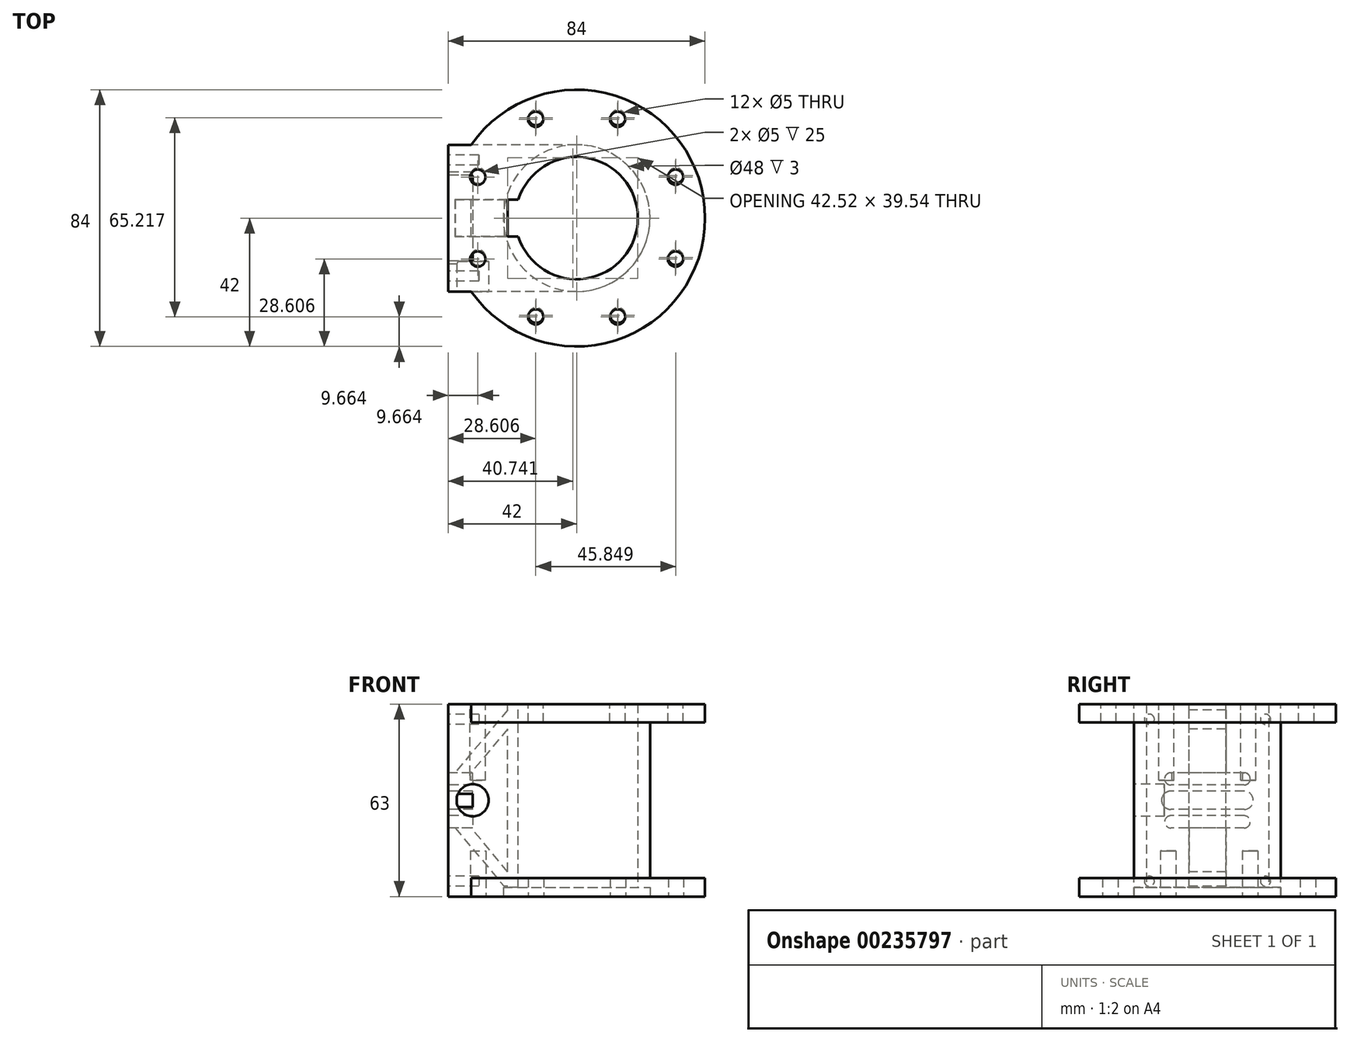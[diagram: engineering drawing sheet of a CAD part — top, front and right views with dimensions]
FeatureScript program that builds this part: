
annotation { "Feature Type Name" : "Feature", "Feature Type Description" : "" }
export const myFeature = defineFeature(function(context is Context, id is Id, definition is map)
    precondition{}
    {
        {
            var Q0;
            Q0=qCreatedBy(makeId("Top.planeOp"),FACE);
            var sketch = newSketch(context, id + "F0", { "sketchPlane" : qUnion([Q0])});
            skCircle(sketch, "E0", {"center": v(0, 0) * mm, "radius": 42 * mm});
            skSolve(sketch);
        }
        {
            var Q0;
            Q0=makeQuery(id+"F0.imprint","IMPRINT",FACE,{"disambiguationData":[TD([[makeQuery(id+"F0.imprint","IMPRINT",EDGE,{"derivedFrom":sQuery(id+"F0.wireOp",EDGE,"E0")}),1.0]])]});
            extrude(context, id + "F1", {"entities" : qUnion([Q0]), "depth" : 6 * mm});
        }
        {
            var Q0;
            Q0=makeQuery(id+"F1.opExtrude","CAP_FACE",FACE,{"disambiguationData":[OSD([sQuery(id+"F0.wireOp",EDGE,"E0")])],"isStart":false});
            var sketch = newSketch(context, id + "F2", { "sketchPlane" : qUnion([Q0])});
            skCircle(sketch, "E1", {"center": v(0, 0) * mm, "radius": 24 * mm});
            skLineSegment(sketch, "E2", {"start": v(0, 24) * mm, "end": v(-42, 24) * mm});
            skLineSegment(sketch, "E3.MirrorCS", {"start": v(0, -24) * mm, "end": v(-42, -24) * mm});
            skLineSegment(sketch, "E4", {"start": v(-42, 24) * mm, "end": v(-42, -24) * mm});
            skSolve(sketch);
        }
        {
            var Q0;
            {var subQ0=sQuery(id+"F2.wireOp",EDGE,"E4");var subQ1=sQuery(id+"F2.wireOp",EDGE,"E2");var subQ2=makeQuery(id+"F2.imprint","INTERSECT",VERTEX,{"derivedFrom":[subQ1,subQ0]});Q0=makeQuery(id+"F2.imprint","IMPRINT",FACE,{"disambiguationData":[TD([[makeQuery(id+"F2.imprint","IMPRINT",EDGE,{"disambiguationData":[TD([[subQ2,1.0]])],"derivedFrom":subQ1}),1.0]])]});}
            var Q1;
            {var subQ0=sQuery(id+"F2.wireOp",EDGE,"E4");var subQ1=sQuery(id+"F2.wireOp",EDGE,"E3.MirrorCS");var subQ2=makeQuery(id+"F2.imprint","INTERSECT",VERTEX,{"derivedFrom":[subQ1,subQ0]});Q1=makeQuery(id+"F2.imprint","IMPRINT",FACE,{"disambiguationData":[TD([[makeQuery(id+"F2.imprint","IMPRINT",EDGE,{"disambiguationData":[TD([[subQ2,1.0]])],"derivedFrom":subQ1}),-1.0]])]});}
            extrude(context, id + "F3", {"entities" : qUnion([Q0, Q1]), "operationType" : NewBodyOperationType.ADD, "oppositeDirection" : true, "depth" : 6 * mm});
        }
        {
            var Q0;
            {var subQ0=sQuery(id+"F2.wireOp",EDGE,"E1");var subQ1=makeQuery(id+"F2.imprint","INTERSECT",VERTEX,{"derivedFrom":[subQ0,sQuery(id+"F2.wireOp",EDGE,"E2")]});Q0=makeQuery(id+"F2.imprint","IMPRINT",FACE,{"disambiguationData":[TD([[makeQuery(id+"F2.imprint","IMPRINT",EDGE,{"disambiguationData":[TD([[subQ1,-1.0]])],"derivedFrom":subQ0}),1.0]])]});}
            var Q1;
            {var subQ1=sQuery(id+"F2.wireOp",EDGE,"E1");var subQ6=sQuery(id+"F2.wireOp",EDGE,"E2");var subQ8=makeQuery(id+"F2.imprint","INTERSECT",VERTEX,{"derivedFrom":[subQ1,subQ6]});Q1=makeQuery(id+"F2.imprint","IMPRINT",FACE,{"disambiguationData":[TD([[makeQuery(id+"F2.imprint","IMPRINT",EDGE,{"disambiguationData":[TD([[subQ8,-1.0]])],"derivedFrom":subQ1}),-1.0]])]});}
            var Q2;
            {var subQ0=sQuery(id+"F2.wireOp",EDGE,"E4");var subQ1=sQuery(id+"F2.wireOp",EDGE,"E3.MirrorCS");var subQ2=makeQuery(id+"F2.imprint","INTERSECT",VERTEX,{"derivedFrom":[subQ1,subQ0]});Q2=makeQuery(id+"F2.imprint","IMPRINT",FACE,{"disambiguationData":[TD([[makeQuery(id+"F2.imprint","IMPRINT",EDGE,{"disambiguationData":[TD([[subQ2,1.0]])],"derivedFrom":subQ1}),-1.0]])]});}
            var Q3;
            {var subQ0=sQuery(id+"F2.wireOp",EDGE,"E4");var subQ1=sQuery(id+"F2.wireOp",EDGE,"E2");var subQ2=makeQuery(id+"F2.imprint","INTERSECT",VERTEX,{"derivedFrom":[subQ1,subQ0]});Q3=makeQuery(id+"F2.imprint","IMPRINT",FACE,{"disambiguationData":[TD([[makeQuery(id+"F2.imprint","IMPRINT",EDGE,{"disambiguationData":[TD([[subQ2,1.0]])],"derivedFrom":subQ1}),1.0]])]});}
            extrude(context, id + "F4", {"entities" : qUnion([Q0, Q1, Q2, Q3]), "operationType" : NewBodyOperationType.ADD, "depth" : 57 * mm});
        }
        {
            var Q0;
            Q0=makeQuery(id+"F4.opExtrude","CAP_FACE",FACE,{"disambiguationData":[OSD([sQuery(id+"F2.wireOp",EDGE,"E1"),sQuery(id+"F2.wireOp",EDGE,"E2"),sQuery(id+"F2.wireOp",EDGE,"E3.MirrorCS"),sQuery(id+"F2.wireOp",EDGE,"E4")])],"isStart":false});
            var sketch = newSketch(context, id + "F5", { "sketchPlane" : qUnion([Q0])});
            skCircle(sketch, "E5", {"center": v(0, 0) * mm, "radius": 42 * mm});
            skSolve(sketch);
        }
        {
            var Q0;
            {var subQ5=makeQuery(id+"F4.opExtrude","CAP_EDGE",EDGE,{"disambiguationData":[OSD([sQuery(id+"F2.wireOp",EDGE,"E1")])],"isStart":false});Q0=makeQuery(id+"F5.imprint","IMPRINT",FACE,{"disambiguationData":[TD([[makeQuery(id+"F5.imprint","IMPRINT",EDGE,{"derivedFrom":subQ5}),-1.0]])]});}
            extrude(context, id + "F6", {"entities" : qUnion([Q0]), "operationType" : NewBodyOperationType.ADD, "oppositeDirection" : true, "depth" : 6 * mm});
        }
        {
            var Q0;
            {var subQ0=sQuery(id+"F2.wireOp",EDGE,"E4");var subQ1=sQuery(id+"F0.wireOp",EDGE,"E0");Q0=makeQuery(id+"F3.boolean.opBoolean","MERGE",FACE,{"derivedFrom":[makeQuery(id+"F1.opExtrude","CAP_FACE",FACE,{"disambiguationData":[OSD([subQ1])],"isStart":true}),makeQuery(id+"F3.opExtrude","CAP_FACE",FACE,{"disambiguationData":[OSD([subQ1,sQuery(id+"F2.wireOp",EDGE,"E2"),subQ0])],"isStart":false}),makeQuery(id+"F3.opExtrude","CAP_FACE",FACE,{"disambiguationData":[OSD([subQ1,sQuery(id+"F2.wireOp",EDGE,"E3.MirrorCS"),subQ0])],"isStart":false})]});}
            var sketch = newSketch(context, id + "F7", { "sketchPlane" : qUnion([Q0])});
            skPoint(sketch, "E6", {"position": v(0, 0) * mm});
            skSolve(sketch);
        }
        {
            var Q0;
            Q0=sQuery(id+"F7.wireOp",VERTEX,"E6");
            var Q1;
            Q1=makeQuery(id+"F1.opExtrude","SWEPT_BODY",BODY,{"disambiguationData":[OSD([sQuery(id+"F0.wireOp",EDGE,"E0")])]});
            hole(context, id + "F8", {"style" : HoleStyle.C_BORE, "endStyle" : HoleEndStyle.BLIND, "holeDiameter" : 40 * mm, "cBoreDiameter" : 48 * mm, "cBoreDepth" : 3 * mm, "holeDepth" : 63 * mm, "tappedDepth" : 20 * mm, "tapClearance" : 6, "startFromSketch" : true, "locations" : qUnion([Q0]), "scope" : qUnion([Q1])});
        }
        {
            var Q0;
            {var subQ0=sQuery(id+"F2.wireOp",EDGE,"E4");Q0=makeQuery(id+"F4.boolean.opBoolean","MERGE",FACE,{"derivedFrom":[makeQuery(id+"F3.boolean.opBoolean","MERGE",FACE,{"derivedFrom":[makeQuery(id+"F3.opExtrude","SWEPT_FACE",FACE,{"disambiguationData":[OSD([subQ0]),TDD([makeQuery(id+"F2.imprint","IMPRINT",EDGE,{"disambiguationData":[TD([[makeQuery(id+"F2.imprint","INTERSECT",VERTEX,{"derivedFrom":[sQuery(id+"F2.wireOp",EDGE,"E2"),subQ0]}),-1.0]])],"derivedFrom":subQ0})])]}),makeQuery(id+"F3.opExtrude","SWEPT_FACE",FACE,{"disambiguationData":[OSD([subQ0]),TDD([makeQuery(id+"F2.imprint","IMPRINT",EDGE,{"disambiguationData":[TD([[makeQuery(id+"F2.imprint","INTERSECT",VERTEX,{"derivedFrom":[sQuery(id+"F2.wireOp",EDGE,"E3.MirrorCS"),subQ0]}),1.0]])],"derivedFrom":subQ0})])]})]}),makeQuery(id+"F4.opExtrude","SWEPT_FACE",FACE,{"disambiguationData":[OSD([subQ0])]})]});}
            var sketch = newSketch(context, id + "F9", { "sketchPlane" : qUnion([Q0])});
            skLineSegment(sketch, "E7", {"start": v(0, 0) * mm, "end": v(19, 0) * mm});
            skLineSegment(sketch, "E8.MirrorCS", {"start": v(0, 0) * mm, "end": v(-19, 0) * mm});
            skPoint(sketch, "E9.startSnap0", {"position": v(24, 31.5) * mm});
            skLineSegment(sketch, "E10", {"start": v(19, 5) * mm, "end": v(19, 58) * mm});
            skLineSegment(sketch, "E11", {"start": v(19, 58) * mm, "end": v(-19, 58) * mm});
            skLineSegment(sketch, "E12", {"start": v(-19, 5) * mm, "end": v(19, 5) * mm});
            skLineSegment(sketch, "E13", {"start": v(-19, 58) * mm, "end": v(-19, 5) * mm});
            skCircle(sketch, "E14", {"center": v(19, 58) * mm, "radius": 1.65 * mm});
            skCircle(sketch, "E15", {"center": v(19, 5) * mm, "radius": 1.65 * mm});
            skCircle(sketch, "E16.MirrorC", {"center": v(-19, 58) * mm, "radius": 1.65 * mm});
            skCircle(sketch, "E17.MirrorC", {"center": v(-19, 5) * mm, "radius": 1.65 * mm});
            skPoint(sketch, "E18.startSnap0", {"position": v(19, 31.5) * mm});
            skPoint(sketch, "E18.endSnap0", {"position": v(19, 31.5) * mm});
            skLineSegment(sketch, "E19", {"start": v(-12, 34.5) * mm, "end": v(12, 34.5) * mm});
            skLineSegment(sketch, "E20", {"start": v(-12, 28.5) * mm, "end": v(12, 28.5) * mm});
            skArc(sketch, "E21", {"start": v(-12, 28.5) * mm, "mid": v(-15, 31.5) * mm, "end": v(-12, 34.5) * mm});
            skArc(sketch, "E22", {"start": v(12, 28.5) * mm, "mid": v(15, 31.5) * mm, "end": v(12, 34.5) * mm});
            skLineSegment(sketch, "E23", {"start": v(-12, 40.5) * mm, "end": v(12, 40.5) * mm});
            skLineSegment(sketch, "E24", {"start": v(-12, 36.5) * mm, "end": v(12, 36.5) * mm});
            skArc(sketch, "E25", {"start": v(-12, 36.5) * mm, "mid": v(-14, 38.5) * mm, "end": v(-12, 40.5) * mm});
            skArc(sketch, "E26", {"start": v(12, 36.5) * mm, "mid": v(14, 38.5) * mm, "end": v(12, 40.5) * mm});
            skLineSegment(sketch, "E27", {"start": v(-12, 26.44) * mm, "end": v(12, 26.44) * mm});
            skLineSegment(sketch, "E28", {"start": v(-12, 22.44) * mm, "end": v(12, 22.44) * mm});
            skArc(sketch, "E29", {"start": v(-12, 22.44) * mm, "mid": v(-14, 24.44) * mm, "end": v(-12, 26.44) * mm});
            skArc(sketch, "E30", {"start": v(12, 22.44) * mm, "mid": v(14, 24.44) * mm, "end": v(12, 26.44) * mm});
            skSolve(sketch);
        }
        {
            var Q0;
            Q0=makeQuery(id+"F9.imprint","IMPRINT",FACE,{"disambiguationData":[TD([[makeQuery(id+"F9.imprint","IMPRINT",EDGE,{"derivedFrom":sQuery(id+"F9.wireOp",EDGE,"E23")}),-1.0]])]});
            var Q1;
            Q1=makeQuery(id+"F9.imprint","IMPRINT",FACE,{"disambiguationData":[TD([[makeQuery(id+"F9.imprint","IMPRINT",EDGE,{"derivedFrom":sQuery(id+"F9.wireOp",EDGE,"E19")}),-1.0]])]});
            var Q2;
            Q2=makeQuery(id+"F9.imprint","IMPRINT",FACE,{"disambiguationData":[TD([[makeQuery(id+"F9.imprint","IMPRINT",EDGE,{"derivedFrom":sQuery(id+"F9.wireOp",EDGE,"E27")}),-1.0]])]});
            extrude(context, id + "F10", {"entities" : qUnion([Q0, Q1, Q2]), "operationType" : NewBodyOperationType.REMOVE, "oppositeDirection" : true, "depth" : 8 * mm});
        }
        {
            var Q0;
            {var subQ0=sQuery(id+"F9.wireOp",EDGE,"E13");var subQ1=sQuery(id+"F9.wireOp",EDGE,"E12");var subQ2=makeQuery(id+"F9.imprint","INTERSECT",VERTEX,{"derivedFrom":[subQ1,subQ0]});Q0=makeQuery(id+"F9.imprint","IMPRINT",FACE,{"disambiguationData":[TD([[makeQuery(id+"F9.imprint","IMPRINT",EDGE,{"disambiguationData":[TD([[subQ2,-1.0]])],"derivedFrom":subQ1}),-1.0]])]});}
            var Q1;
            {var subQ0=sQuery(id+"F9.wireOp",EDGE,"E13");var subQ1=sQuery(id+"F9.wireOp",EDGE,"E12");var subQ2=makeQuery(id+"F9.imprint","INTERSECT",VERTEX,{"derivedFrom":[subQ1,subQ0]});Q1=makeQuery(id+"F9.imprint","IMPRINT",FACE,{"disambiguationData":[TD([[makeQuery(id+"F9.imprint","IMPRINT",EDGE,{"disambiguationData":[TD([[subQ2,-1.0]])],"derivedFrom":subQ1}),1.0]])]});}
            var Q2;
            {var subQ0=sQuery(id+"F9.wireOp",EDGE,"E12");var subQ1=sQuery(id+"F9.wireOp",EDGE,"E10");var subQ2=makeQuery(id+"F9.imprint","INTERSECT",VERTEX,{"derivedFrom":[subQ1,subQ0]});Q2=makeQuery(id+"F9.imprint","IMPRINT",FACE,{"disambiguationData":[TD([[makeQuery(id+"F9.imprint","IMPRINT",EDGE,{"disambiguationData":[TD([[subQ2,-1.0]])],"derivedFrom":subQ1}),-1.0]])]});}
            var Q3;
            {var subQ0=sQuery(id+"F9.wireOp",EDGE,"E12");var subQ1=sQuery(id+"F9.wireOp",EDGE,"E10");var subQ2=makeQuery(id+"F9.imprint","INTERSECT",VERTEX,{"derivedFrom":[subQ1,subQ0]});Q3=makeQuery(id+"F9.imprint","IMPRINT",FACE,{"disambiguationData":[TD([[makeQuery(id+"F9.imprint","IMPRINT",EDGE,{"disambiguationData":[TD([[subQ2,-1.0]])],"derivedFrom":subQ1}),1.0]])]});}
            var Q4;
            {var subQ0=sQuery(id+"F9.wireOp",EDGE,"E11");var subQ1=sQuery(id+"F9.wireOp",EDGE,"E10");var subQ2=makeQuery(id+"F9.imprint","INTERSECT",VERTEX,{"derivedFrom":[subQ1,subQ0]});Q4=makeQuery(id+"F9.imprint","IMPRINT",FACE,{"disambiguationData":[TD([[makeQuery(id+"F9.imprint","IMPRINT",EDGE,{"disambiguationData":[TD([[subQ2,1.0]])],"derivedFrom":subQ1}),1.0]])]});}
            var Q5;
            {var subQ0=sQuery(id+"F9.wireOp",EDGE,"E11");var subQ1=sQuery(id+"F9.wireOp",EDGE,"E10");var subQ2=makeQuery(id+"F9.imprint","INTERSECT",VERTEX,{"derivedFrom":[subQ1,subQ0]});Q5=makeQuery(id+"F9.imprint","IMPRINT",FACE,{"disambiguationData":[TD([[makeQuery(id+"F9.imprint","IMPRINT",EDGE,{"disambiguationData":[TD([[subQ2,1.0]])],"derivedFrom":subQ1}),-1.0]])]});}
            var Q6;
            {var subQ0=sQuery(id+"F9.wireOp",EDGE,"E13");var subQ1=sQuery(id+"F9.wireOp",EDGE,"E11");var subQ2=makeQuery(id+"F9.imprint","INTERSECT",VERTEX,{"derivedFrom":[subQ1,subQ0]});Q6=makeQuery(id+"F9.imprint","IMPRINT",FACE,{"disambiguationData":[TD([[makeQuery(id+"F9.imprint","IMPRINT",EDGE,{"disambiguationData":[TD([[subQ2,1.0]])],"derivedFrom":subQ1}),1.0]])]});}
            var Q7;
            {var subQ0=sQuery(id+"F9.wireOp",EDGE,"E13");var subQ1=sQuery(id+"F9.wireOp",EDGE,"E11");var subQ2=makeQuery(id+"F9.imprint","INTERSECT",VERTEX,{"derivedFrom":[subQ1,subQ0]});Q7=makeQuery(id+"F9.imprint","IMPRINT",FACE,{"disambiguationData":[TD([[makeQuery(id+"F9.imprint","IMPRINT",EDGE,{"disambiguationData":[TD([[subQ2,1.0]])],"derivedFrom":subQ1}),-1.0]])]});}
            extrude(context, id + "F11", {"entities" : qUnion([Q0, Q1, Q2, Q3, Q4, Q5, Q6, Q7]), "operationType" : NewBodyOperationType.REMOVE, "oppositeDirection" : true, "depth" : 10 * mm});
        }
        {
            var Q0;
            {var subQ0=sQuery(id+"F2.wireOp",EDGE,"E3.MirrorCS");var subQ1=sQuery(id+"F2.wireOp",EDGE,"E2");var subQ2=sQuery(id+"F2.wireOp",EDGE,"E1");Q0=makeQuery(id+"F6.boolean.opBoolean","MERGE",FACE,{"derivedFrom":[makeQuery(id+"F4.opExtrude","CAP_FACE",FACE,{"disambiguationData":[OSD([subQ2,subQ1,subQ0,sQuery(id+"F2.wireOp",EDGE,"E4")])],"isStart":false}),makeQuery(id+"F6.opExtrude","CAP_FACE",FACE,{"disambiguationData":[OSD([subQ2,subQ1,subQ0,sQuery(id+"F5.wireOp",EDGE,"E5")])],"isStart":true})]});}
            var sketch = newSketch(context, id + "F12", { "sketchPlane" : qUnion([Q0])});
            skLineSegment(sketch, "E31", {"start": v(-20, 6) * mm, "end": v(-19.08, 6) * mm});
            skLineSegment(sketch, "E32", {"start": v(-20, -6) * mm, "end": v(-19.08, -6) * mm});
            skLineSegment(sketch, "E33", {"start": v(-19.08, -6) * mm, "end": v(-22.52, -6) * mm});
            skLineSegment(sketch, "E34.MirrorCS", {"start": v(-19.08, 6) * mm, "end": v(-22.52, 6) * mm});
            skLineSegment(sketch, "E35", {"start": v(-22.52, 6) * mm, "end": v(-22.52, -6) * mm});
            skSolve(sketch);
        }
        {
            var Q0;
            {var subQ0=sQuery(id+"F12.wireOp",EDGE,"E35");Q0=makeQuery(id+"F12.imprint","IMPRINT",FACE,{"disambiguationData":[TD([[makeQuery(id+"F12.imprint","IMPRINT",EDGE,{"derivedFrom":subQ0}),1.0]])]});}
            extrude(context, id + "F13", {"entities" : qUnion([Q0]), "operationType" : NewBodyOperationType.REMOVE, "endBound" : BoundingType.THROUGH_ALL, "oppositeDirection" : true, "depth" : 25 * mm});
        }
        {
            var Q0;
            {var subQ0=sQuery(id+"F2.wireOp",EDGE,"E3.MirrorCS");var subQ1=sQuery(id+"F2.wireOp",EDGE,"E2");var subQ2=sQuery(id+"F2.wireOp",EDGE,"E1");Q0=makeQuery(id+"F6.boolean.opBoolean","MERGE",FACE,{"derivedFrom":[makeQuery(id+"F4.opExtrude","CAP_FACE",FACE,{"disambiguationData":[OSD([subQ2,subQ1,subQ0,sQuery(id+"F2.wireOp",EDGE,"E4")])],"isStart":false}),makeQuery(id+"F6.opExtrude","CAP_FACE",FACE,{"disambiguationData":[OSD([subQ2,subQ1,subQ0,sQuery(id+"F5.wireOp",EDGE,"E5")])],"isStart":true})]});}
            var sketch = newSketch(context, id + "F14", { "sketchPlane" : qUnion([Q0])});
            skCircle(sketch, "E36", {"center": v(0, 0) * mm, "radius": 35 * mm});
            skCircle(sketch, "E37", {"center": v(-32.34, 13.4) * mm, "radius": 2.5 * mm});
            skCircle(sketch, "E38.1.1", {"center": v(-32.34, -13.4) * mm, "radius": 2.5 * mm});
            skCircle(sketch, "E38.2.1", {"center": v(-13.4, -32.34) * mm, "radius": 2.5 * mm});
            skCircle(sketch, "E38.3.1", {"center": v(13.4, -32.34) * mm, "radius": 2.5 * mm});
            skCircle(sketch, "E38.4.1", {"center": v(32.34, -13.4) * mm, "radius": 2.5 * mm});
            skCircle(sketch, "E38.5.1", {"center": v(32.34, 13.4) * mm, "radius": 2.5 * mm});
            skCircle(sketch, "E38.6.1", {"center": v(13.4, 32.34) * mm, "radius": 2.5 * mm});
            skCircle(sketch, "E38.7.1", {"center": v(-13.4, 32.34) * mm, "radius": 2.5 * mm});
            skSolve(sketch);
        }
        {
            var Q0;
            {var subQ0=sQuery(id+"F2.wireOp",EDGE,"E4");var subQ1=sQuery(id+"F0.wireOp",EDGE,"E0");Q0=makeQuery(id+"F3.boolean.opBoolean","MERGE",FACE,{"derivedFrom":[makeQuery(id+"F1.opExtrude","CAP_FACE",FACE,{"disambiguationData":[OSD([subQ1])],"isStart":true}),makeQuery(id+"F3.opExtrude","CAP_FACE",FACE,{"disambiguationData":[OSD([subQ1,sQuery(id+"F2.wireOp",EDGE,"E2"),subQ0])],"isStart":false}),makeQuery(id+"F3.opExtrude","CAP_FACE",FACE,{"disambiguationData":[OSD([subQ1,sQuery(id+"F2.wireOp",EDGE,"E3.MirrorCS"),subQ0])],"isStart":false})]});}
            var sketch = newSketch(context, id + "F15", { "sketchPlane" : qUnion([Q0])});
            skCircle(sketch, "E39", {"center": v(0.12, -0.55) * mm, "radius": 35 * mm});
            skLineSegment(sketch, "E40", {"start": v(0.12, -0.55) * mm, "end": v(-52.54, 21.27) * mm});
            skCircle(sketch, "E41", {"center": v(-32.22, 12.85) * mm, "radius": 2.5 * mm});
            skCircle(sketch, "E42.1.1", {"center": v(-32.22, -13.94) * mm, "radius": 2.5 * mm});
            skCircle(sketch, "E42.2.1", {"center": v(-13.27, -32.88) * mm, "radius": 2.5 * mm});
            skCircle(sketch, "E42.3.1", {"center": v(13.51, -32.88) * mm, "radius": 2.5 * mm});
            skCircle(sketch, "E42.4.1", {"center": v(32.45, -13.94) * mm, "radius": 2.5 * mm});
            skCircle(sketch, "E42.5.1", {"center": v(32.45, 12.85) * mm, "radius": 2.5 * mm});
            skCircle(sketch, "E42.6.1", {"center": v(13.51, 31.8) * mm, "radius": 2.5 * mm});
            skCircle(sketch, "E42.7.1", {"center": v(-13.27, 31.8) * mm, "radius": 2.5 * mm});
            skSolve(sketch);
        }
        {
            var Q0;
            {var subQ0=sQuery(id+"F15.wireOp",EDGE,"E42.8.1");var subQ1=sQuery(id+"F15.wireOp",EDGE,"E42.8.0");var subQ2=makeQuery(id+"F15.imprint","INTERSECT",VERTEX,{"disambiguationData":[OD(0.0)],"derivedFrom":[subQ1,subQ0]});Q0=makeQuery(id+"F15.imprint","IMPRINT",FACE,{"disambiguationData":[TD([[makeQuery(id+"F15.imprint","IMPRINT",EDGE,{"disambiguationData":[TD([[subQ2,-1.0]])],"derivedFrom":subQ1}),-1.0]])]});}
            var Q1;
            {var subQ0=sQuery(id+"F15.wireOp",EDGE,"E42.8.1");var subQ1=sQuery(id+"F15.wireOp",EDGE,"E42.8.0");var subQ2=makeQuery(id+"F15.imprint","INTERSECT",VERTEX,{"disambiguationData":[OD(0.0)],"derivedFrom":[subQ1,subQ0]});Q1=makeQuery(id+"F15.imprint","IMPRINT",FACE,{"disambiguationData":[TD([[makeQuery(id+"F15.imprint","IMPRINT",EDGE,{"disambiguationData":[TD([[subQ2,-1.0]])],"derivedFrom":subQ1}),1.0]])]});}
            var Q2;
            {var subQ0=sQuery(id+"F15.wireOp",EDGE,"E42.8.0");var subQ1=sQuery(id+"F15.wireOp",EDGE,"E42.7.1");var subQ2=makeQuery(id+"F15.imprint","INTERSECT",VERTEX,{"disambiguationData":[OD(0.0)],"derivedFrom":[subQ1,subQ0]});Q2=makeQuery(id+"F15.imprint","IMPRINT",FACE,{"disambiguationData":[TD([[makeQuery(id+"F15.imprint","IMPRINT",EDGE,{"disambiguationData":[TD([[subQ2,-1.0]])],"derivedFrom":subQ1}),1.0]])]});}
            var Q3;
            {var subQ0=sQuery(id+"F15.wireOp",EDGE,"E42.8.0");var subQ1=sQuery(id+"F15.wireOp",EDGE,"E42.7.1");var subQ2=makeQuery(id+"F15.imprint","INTERSECT",VERTEX,{"disambiguationData":[OD(0.0)],"derivedFrom":[subQ1,subQ0]});Q3=makeQuery(id+"F15.imprint","IMPRINT",FACE,{"disambiguationData":[TD([[makeQuery(id+"F15.imprint","IMPRINT",EDGE,{"disambiguationData":[TD([[subQ2,1.0]])],"derivedFrom":subQ1}),1.0]])]});}
            var Q4;
            {var subQ0=sQuery(id+"F15.wireOp",EDGE,"E42.8.0");var subQ1=sQuery(id+"F15.wireOp",EDGE,"E42.6.1");var subQ2=makeQuery(id+"F15.imprint","INTERSECT",VERTEX,{"disambiguationData":[OD(0.0)],"derivedFrom":[subQ1,subQ0]});Q4=makeQuery(id+"F15.imprint","IMPRINT",FACE,{"disambiguationData":[TD([[makeQuery(id+"F15.imprint","IMPRINT",EDGE,{"disambiguationData":[TD([[subQ2,-1.0]])],"derivedFrom":subQ1}),1.0]])]});}
            var Q5;
            {var subQ0=sQuery(id+"F15.wireOp",EDGE,"E42.8.0");var subQ1=sQuery(id+"F15.wireOp",EDGE,"E42.6.1");var subQ2=makeQuery(id+"F15.imprint","INTERSECT",VERTEX,{"disambiguationData":[OD(0.0)],"derivedFrom":[subQ1,subQ0]});Q5=makeQuery(id+"F15.imprint","IMPRINT",FACE,{"disambiguationData":[TD([[makeQuery(id+"F15.imprint","IMPRINT",EDGE,{"disambiguationData":[TD([[subQ2,1.0]])],"derivedFrom":subQ1}),1.0]])]});}
            var Q6;
            {var subQ0=sQuery(id+"F15.wireOp",EDGE,"E42.8.0");var subQ1=sQuery(id+"F15.wireOp",EDGE,"E42.5.1");var subQ2=makeQuery(id+"F15.imprint","INTERSECT",VERTEX,{"disambiguationData":[OD(0.0)],"derivedFrom":[subQ1,subQ0]});Q6=makeQuery(id+"F15.imprint","IMPRINT",FACE,{"disambiguationData":[TD([[makeQuery(id+"F15.imprint","IMPRINT",EDGE,{"disambiguationData":[TD([[subQ2,-1.0]])],"derivedFrom":subQ1}),1.0]])]});}
            var Q7;
            {var subQ0=sQuery(id+"F15.wireOp",EDGE,"E42.8.0");var subQ1=sQuery(id+"F15.wireOp",EDGE,"E42.5.1");var subQ2=makeQuery(id+"F15.imprint","INTERSECT",VERTEX,{"disambiguationData":[OD(0.0)],"derivedFrom":[subQ1,subQ0]});Q7=makeQuery(id+"F15.imprint","IMPRINT",FACE,{"disambiguationData":[TD([[makeQuery(id+"F15.imprint","IMPRINT",EDGE,{"disambiguationData":[TD([[subQ2,1.0]])],"derivedFrom":subQ1}),1.0]])]});}
            var Q8;
            {var subQ0=sQuery(id+"F15.wireOp",EDGE,"E42.8.0");var subQ1=sQuery(id+"F15.wireOp",EDGE,"E42.4.1");var subQ2=makeQuery(id+"F15.imprint","INTERSECT",VERTEX,{"disambiguationData":[OD(0.0)],"derivedFrom":[subQ1,subQ0]});Q8=makeQuery(id+"F15.imprint","IMPRINT",FACE,{"disambiguationData":[TD([[makeQuery(id+"F15.imprint","IMPRINT",EDGE,{"disambiguationData":[TD([[subQ2,1.0]])],"derivedFrom":subQ1}),1.0]])]});}
            var Q9;
            {var subQ0=sQuery(id+"F15.wireOp",EDGE,"E42.8.0");var subQ1=sQuery(id+"F15.wireOp",EDGE,"E42.4.1");var subQ2=makeQuery(id+"F15.imprint","INTERSECT",VERTEX,{"disambiguationData":[OD(0.0)],"derivedFrom":[subQ1,subQ0]});Q9=makeQuery(id+"F15.imprint","IMPRINT",FACE,{"disambiguationData":[TD([[makeQuery(id+"F15.imprint","IMPRINT",EDGE,{"disambiguationData":[TD([[subQ2,-1.0]])],"derivedFrom":subQ1}),1.0]])]});}
            var Q10;
            {var subQ0=sQuery(id+"F15.wireOp",EDGE,"E42.8.0");var subQ1=sQuery(id+"F15.wireOp",EDGE,"E42.3.1");var subQ2=makeQuery(id+"F15.imprint","INTERSECT",VERTEX,{"disambiguationData":[OD(0.0)],"derivedFrom":[subQ1,subQ0]});Q10=makeQuery(id+"F15.imprint","IMPRINT",FACE,{"disambiguationData":[TD([[makeQuery(id+"F15.imprint","IMPRINT",EDGE,{"disambiguationData":[TD([[subQ2,-1.0]])],"derivedFrom":subQ1}),1.0]])]});}
            var Q11;
            {var subQ0=sQuery(id+"F15.wireOp",EDGE,"E42.8.0");var subQ1=sQuery(id+"F15.wireOp",EDGE,"E42.3.1");var subQ2=makeQuery(id+"F15.imprint","INTERSECT",VERTEX,{"disambiguationData":[OD(0.0)],"derivedFrom":[subQ1,subQ0]});Q11=makeQuery(id+"F15.imprint","IMPRINT",FACE,{"disambiguationData":[TD([[makeQuery(id+"F15.imprint","IMPRINT",EDGE,{"disambiguationData":[TD([[subQ2,1.0]])],"derivedFrom":subQ1}),1.0]])]});}
            var Q12;
            {var subQ0=sQuery(id+"F15.wireOp",EDGE,"E42.8.0");var subQ1=sQuery(id+"F15.wireOp",EDGE,"E42.2.1");var subQ2=makeQuery(id+"F15.imprint","INTERSECT",VERTEX,{"disambiguationData":[OD(0.0)],"derivedFrom":[subQ1,subQ0]});Q12=makeQuery(id+"F15.imprint","IMPRINT",FACE,{"disambiguationData":[TD([[makeQuery(id+"F15.imprint","IMPRINT",EDGE,{"disambiguationData":[TD([[subQ2,1.0]])],"derivedFrom":subQ1}),1.0]])]});}
            var Q13;
            {var subQ0=sQuery(id+"F15.wireOp",EDGE,"E42.8.0");var subQ1=sQuery(id+"F15.wireOp",EDGE,"E42.2.1");var subQ2=makeQuery(id+"F15.imprint","INTERSECT",VERTEX,{"disambiguationData":[OD(0.0)],"derivedFrom":[subQ1,subQ0]});Q13=makeQuery(id+"F15.imprint","IMPRINT",FACE,{"disambiguationData":[TD([[makeQuery(id+"F15.imprint","IMPRINT",EDGE,{"disambiguationData":[TD([[subQ2,-1.0]])],"derivedFrom":subQ1}),1.0]])]});}
            var Q14;
            {var subQ0=sQuery(id+"F15.wireOp",EDGE,"E42.8.0");var subQ1=sQuery(id+"F15.wireOp",EDGE,"E42.1.1");var subQ2=makeQuery(id+"F15.imprint","INTERSECT",VERTEX,{"disambiguationData":[OD(0.0)],"derivedFrom":[subQ1,subQ0]});Q14=makeQuery(id+"F15.imprint","IMPRINT",FACE,{"disambiguationData":[TD([[makeQuery(id+"F15.imprint","IMPRINT",EDGE,{"disambiguationData":[TD([[subQ2,-1.0]])],"derivedFrom":subQ1}),1.0]])]});}
            var Q15;
            {var subQ0=sQuery(id+"F15.wireOp",EDGE,"E42.8.0");var subQ1=sQuery(id+"F15.wireOp",EDGE,"E42.1.1");var subQ2=makeQuery(id+"F15.imprint","INTERSECT",VERTEX,{"disambiguationData":[OD(0.0)],"derivedFrom":[subQ1,subQ0]});Q15=makeQuery(id+"F15.imprint","IMPRINT",FACE,{"disambiguationData":[TD([[makeQuery(id+"F15.imprint","IMPRINT",EDGE,{"disambiguationData":[TD([[subQ2,1.0]])],"derivedFrom":subQ1}),1.0]])]});}
            var Q16;
            {var subQ0=sQuery(id+"F15.wireOp",EDGE,"E41");var subQ1=sQuery(id+"F15.wireOp",EDGE,"E40");var subQ2=makeQuery(id+"F15.imprint","INTERSECT",VERTEX,{"disambiguationData":[OD(1.0)],"derivedFrom":[subQ1,subQ0]});Q16=makeQuery(id+"F15.imprint","IMPRINT",FACE,{"disambiguationData":[TD([[makeQuery(id+"F15.imprint","IMPRINT",EDGE,{"disambiguationData":[TD([[subQ2,1.0]])],"derivedFrom":subQ1}),1.0]])]});}
            var Q17;
            {var subQ0=sQuery(id+"F15.wireOp",EDGE,"E41");var subQ1=sQuery(id+"F15.wireOp",EDGE,"E40");var subQ2=makeQuery(id+"F15.imprint","INTERSECT",VERTEX,{"disambiguationData":[OD(1.0)],"derivedFrom":[subQ1,subQ0]});Q17=makeQuery(id+"F15.imprint","IMPRINT",FACE,{"disambiguationData":[TD([[makeQuery(id+"F15.imprint","IMPRINT",EDGE,{"disambiguationData":[TD([[subQ2,1.0]])],"derivedFrom":subQ1}),-1.0]])]});}
            var Q18;
            {var subQ0=sQuery(id+"F15.wireOp",EDGE,"E41");var subQ1=sQuery(id+"F15.wireOp",EDGE,"E40");var subQ2=makeQuery(id+"F15.imprint","INTERSECT",VERTEX,{"disambiguationData":[OD(0.0)],"derivedFrom":[subQ1,subQ0]});Q18=makeQuery(id+"F15.imprint","IMPRINT",FACE,{"disambiguationData":[TD([[makeQuery(id+"F15.imprint","IMPRINT",EDGE,{"disambiguationData":[TD([[subQ2,-1.0]])],"derivedFrom":subQ1}),-1.0]])]});}
            var Q19;
            {var subQ0=sQuery(id+"F15.wireOp",EDGE,"E41");var subQ1=sQuery(id+"F15.wireOp",EDGE,"E40");var subQ2=makeQuery(id+"F15.imprint","INTERSECT",VERTEX,{"disambiguationData":[OD(0.0)],"derivedFrom":[subQ1,subQ0]});Q19=makeQuery(id+"F15.imprint","IMPRINT",FACE,{"disambiguationData":[TD([[makeQuery(id+"F15.imprint","IMPRINT",EDGE,{"disambiguationData":[TD([[subQ2,-1.0]])],"derivedFrom":subQ1}),1.0]])]});}
            extrude(context, id + "F16", {"entities" : qUnion([Q0, Q1, Q2, Q3, Q4, Q5, Q6, Q7, Q8, Q9, Q10, Q11, Q12, Q13, Q14, Q15, Q16, Q17, Q18, Q19]), "operationType" : NewBodyOperationType.REMOVE, "oppositeDirection" : true, "depth" : 15 * mm});
        }
        {
            var Q0;
            {var subQ0=sQuery(id+"F2.wireOp",EDGE,"E3.MirrorCS");Q0=makeQuery(id+"F4.boolean.opBoolean","MERGE",FACE,{"derivedFrom":[makeQuery(id+"F3.opExtrude","SWEPT_FACE",FACE,{"disambiguationData":[OSD([subQ0])]}),makeQuery(id+"F4.opExtrude","SWEPT_FACE",FACE,{"disambiguationData":[OSD([subQ0])]})]});}
            var sketch = newSketch(context, id + "F17", { "sketchPlane" : qUnion([Q0])});
            skLineSegment(sketch, "E43", {"start": v(-42, 31.5) * mm, "end": v(-34, 31.5) * mm});
            skPoint(sketch, "E43.endSnap0", {"position": v(-42, 31.5) * mm});
            skCircle(sketch, "E44", {"center": v(-34, 31.5) * mm, "radius": 5.25 * mm});
            skSolve(sketch);
        }
        {
            var Q0;
            Q0=makeQuery(id+"F17.imprint","IMPRINT",FACE,{"disambiguationData":[TD([[makeQuery(id+"F17.imprint","IMPRINT",EDGE,{"derivedFrom":sQuery(id+"F17.wireOp",EDGE,"E44")}),1.0]])]});
            extrude(context, id + "F18", {"entities" : qUnion([Q0]), "operationType" : NewBodyOperationType.REMOVE, "oppositeDirection" : true, "depth" : 9.9 * mm});
        }
        {
            var Q0;
            Q0=qCreatedBy(makeId("Front.planeOp"),FACE);
            var sketch = newSketch(context, id + "F19", { "sketchPlane" : qUnion([Q0])});
            skLineSegment(sketch, "E45", {"start": v(-24.02, 3.7) * mm, "end": v(-39.19, 21.77) * mm});
            skLineSegment(sketch, "E46", {"start": v(-39.19, 21.77) * mm, "end": v(-41.48, 24.5) * mm});
            skLineSegment(sketch, "E47", {"start": v(-31.79, 19.17) * mm, "end": v(-36.26, 24.5) * mm});
            skLineSegment(sketch, "E48", {"start": v(-36.26, 24.5) * mm, "end": v(-23.44, 9.22) * mm});
            skLineSegment(sketch, "E49.MirrorCS", {"start": v(-36.26, 38.5) * mm, "end": v(-23.44, 53.78) * mm});
            skLineSegment(sketch, "E50.MirrorCS", {"start": v(-23.44, 60) * mm, "end": v(-39.19, 41.23) * mm});
            skLineSegment(sketch, "E51", {"start": v(-39.19, 41.23) * mm, "end": v(-41.48, 38.5) * mm});
            skLineSegment(sketch, "E52", {"start": v(-41.48, 24.5) * mm, "end": v(-36.26, 24.5) * mm});
            skLineSegment(sketch, "E53", {"start": v(-42.3, 38.5) * mm, "end": v(-36.26, 38.5) * mm});
            skLineSegment(sketch, "E54", {"start": v(-24.02, 3.7) * mm, "end": v(-23.73, 3.35) * mm});
            skLineSegment(sketch, "E55", {"start": v(-23.44, 9.22) * mm, "end": v(-21.83, 7.3) * mm});
            skLineSegment(sketch, "E56", {"start": v(-23.73, 3.35) * mm, "end": v(-21.83, 3.35) * mm});
            skPoint(sketch, "E56.startSnap0", {"position": v(-23.73, 3.35) * mm});
            skPoint(sketch, "E57.orphan", {"position": v(-23.44, 3) * mm});
            skPoint(sketch, "E58.orphan", {"position": v(-24.02, 3.35) * mm});
            skPoint(sketch, "E59.orphan", {"position": v(-23.44, 0) * mm});
            skLineSegment(sketch, "E60", {"start": v(-21.83, 7.3) * mm, "end": v(-21.83, 3.35) * mm});
            skLineSegment(sketch, "E61", {"start": v(-21.83, 55.7) * mm, "end": v(-21.83, 61.92) * mm});
            skLineSegment(sketch, "E62", {"start": v(-23.44, 60) * mm, "end": v(-21.83, 61.92) * mm});
            skLineSegment(sketch, "E63", {"start": v(-23.44, 53.78) * mm, "end": v(-21.83, 55.7) * mm});
            skSolve(sketch);
        }
        {
            var Q0;
            Q0 = qSketchRegion(id + "F19", true);
            var Q1;
            Q1=makeQuery(id+"F13.boolean.opBoolean","COPY",FACE,{"derivedFrom":makeQuery(id+"F13.opExtrude","SWEPT_FACE",FACE,{"disambiguationData":[OSD([sQuery(id+"F12.wireOp",EDGE,"E34.MirrorCS")])]})});
            var Q2;
            Q2=makeQuery(id+"F13.boolean.opBoolean","COPY",FACE,{"derivedFrom":makeQuery(id+"F13.opExtrude","SWEPT_FACE",FACE,{"disambiguationData":[OSD([sQuery(id+"F12.wireOp",EDGE,"E33")])]})});
            extrude(context, id + "F20", {"entities" : qUnion([Q0]), "operationType" : NewBodyOperationType.REMOVE, "endBound" : BoundingType.UP_TO_SURFACE, "oppositeDirection" : true, "endBoundEntityFace" : qUnion([Q1]), "depth" : 25 * mm, "hasSecondDirection" : true, "secondDirectionBound" : SecondDirectionBoundingType.UP_TO_SURFACE, "secondDirectionOppositeDirection" : false, "secondDirectionBoundEntityFace" : qUnion([Q2]), "secondDirectionDepth" : 25 * mm});
        }
        {
            var Q0;
            Q0 = qSketchRegion(id + "F19", true);
            var Q1;
            Q1=makeQuery(id+"F13.boolean.opBoolean","COPY",FACE,{"derivedFrom":makeQuery(id+"F13.opExtrude","SWEPT_FACE",FACE,{"disambiguationData":[OSD([sQuery(id+"F12.wireOp",EDGE,"E33")])]})});
            extrude(context, id + "F21", {"entities" : qUnion([Q0]), "operationType" : NewBodyOperationType.REMOVE, "endBound" : BoundingType.UP_TO_SURFACE, "endBoundEntityFace" : qUnion([Q1]), "depth" : 25 * mm});
        }
        {
            var Q0;
            {var subQ0=sQuery(id+"F14.wireOp",EDGE,"E36");var subQ1=sQuery(id+"F14.wireOp",EDGE,"E38.3.1");var subQ2=makeQuery(id+"F14.imprint","INTERSECT",VERTEX,{"disambiguationData":[OD(0.0)],"derivedFrom":[subQ1,subQ0]});Q0=makeQuery(id+"F14.imprint","IMPRINT",FACE,{"disambiguationData":[TD([[makeQuery(id+"F14.imprint","IMPRINT",EDGE,{"disambiguationData":[TD([[subQ2,-1.0]])],"derivedFrom":subQ1}),1.0]])]});}
            var Q1;
            {var subQ0=sQuery(id+"F14.wireOp",EDGE,"E36");var subQ1=sQuery(id+"F14.wireOp",EDGE,"E38.3.1");var subQ2=makeQuery(id+"F14.imprint","INTERSECT",VERTEX,{"disambiguationData":[OD(0.0)],"derivedFrom":[subQ1,subQ0]});Q1=makeQuery(id+"F14.imprint","IMPRINT",FACE,{"disambiguationData":[TD([[makeQuery(id+"F14.imprint","IMPRINT",EDGE,{"disambiguationData":[TD([[subQ2,1.0]])],"derivedFrom":subQ1}),1.0]])]});}
            var Q2;
            {var subQ0=sQuery(id+"F14.wireOp",EDGE,"E36");var subQ1=sQuery(id+"F14.wireOp",EDGE,"E38.4.1");var subQ2=makeQuery(id+"F14.imprint","INTERSECT",VERTEX,{"disambiguationData":[OD(0.0)],"derivedFrom":[subQ1,subQ0]});Q2=makeQuery(id+"F14.imprint","IMPRINT",FACE,{"disambiguationData":[TD([[makeQuery(id+"F14.imprint","IMPRINT",EDGE,{"disambiguationData":[TD([[subQ2,1.0]])],"derivedFrom":subQ1}),1.0]])]});}
            var Q3;
            {var subQ0=sQuery(id+"F14.wireOp",EDGE,"E36");var subQ1=sQuery(id+"F14.wireOp",EDGE,"E38.4.1");var subQ2=makeQuery(id+"F14.imprint","INTERSECT",VERTEX,{"disambiguationData":[OD(0.0)],"derivedFrom":[subQ1,subQ0]});Q3=makeQuery(id+"F14.imprint","IMPRINT",FACE,{"disambiguationData":[TD([[makeQuery(id+"F14.imprint","IMPRINT",EDGE,{"disambiguationData":[TD([[subQ2,-1.0]])],"derivedFrom":subQ1}),1.0]])]});}
            var Q4;
            {var subQ0=sQuery(id+"F14.wireOp",EDGE,"E36");var subQ1=sQuery(id+"F14.wireOp",EDGE,"E38.5.1");var subQ2=makeQuery(id+"F14.imprint","INTERSECT",VERTEX,{"disambiguationData":[OD(0.0)],"derivedFrom":[subQ1,subQ0]});Q4=makeQuery(id+"F14.imprint","IMPRINT",FACE,{"disambiguationData":[TD([[makeQuery(id+"F14.imprint","IMPRINT",EDGE,{"disambiguationData":[TD([[subQ2,-1.0]])],"derivedFrom":subQ1}),1.0]])]});}
            var Q5;
            {var subQ0=sQuery(id+"F14.wireOp",EDGE,"E36");var subQ1=sQuery(id+"F14.wireOp",EDGE,"E38.5.1");var subQ2=makeQuery(id+"F14.imprint","INTERSECT",VERTEX,{"disambiguationData":[OD(0.0)],"derivedFrom":[subQ1,subQ0]});Q5=makeQuery(id+"F14.imprint","IMPRINT",FACE,{"disambiguationData":[TD([[makeQuery(id+"F14.imprint","IMPRINT",EDGE,{"disambiguationData":[TD([[subQ2,1.0]])],"derivedFrom":subQ1}),1.0]])]});}
            var Q6;
            {var subQ0=sQuery(id+"F14.wireOp",EDGE,"E36");var subQ1=sQuery(id+"F14.wireOp",EDGE,"E38.6.1");var subQ2=makeQuery(id+"F14.imprint","INTERSECT",VERTEX,{"disambiguationData":[OD(0.0)],"derivedFrom":[subQ1,subQ0]});Q6=makeQuery(id+"F14.imprint","IMPRINT",FACE,{"disambiguationData":[TD([[makeQuery(id+"F14.imprint","IMPRINT",EDGE,{"disambiguationData":[TD([[subQ2,-1.0]])],"derivedFrom":subQ1}),1.0]])]});}
            var Q7;
            {var subQ0=sQuery(id+"F14.wireOp",EDGE,"E36");var subQ1=sQuery(id+"F14.wireOp",EDGE,"E38.6.1");var subQ2=makeQuery(id+"F14.imprint","INTERSECT",VERTEX,{"disambiguationData":[OD(0.0)],"derivedFrom":[subQ1,subQ0]});Q7=makeQuery(id+"F14.imprint","IMPRINT",FACE,{"disambiguationData":[TD([[makeQuery(id+"F14.imprint","IMPRINT",EDGE,{"disambiguationData":[TD([[subQ2,1.0]])],"derivedFrom":subQ1}),1.0]])]});}
            var Q8;
            {var subQ0=sQuery(id+"F14.wireOp",EDGE,"E38.7.1");var subQ1=sQuery(id+"F14.wireOp",EDGE,"E36");var subQ2=makeQuery(id+"F14.imprint","INTERSECT",VERTEX,{"disambiguationData":[OD(0.0)],"derivedFrom":[subQ1,subQ0]});Q8=makeQuery(id+"F14.imprint","IMPRINT",FACE,{"disambiguationData":[TD([[makeQuery(id+"F14.imprint","IMPRINT",EDGE,{"disambiguationData":[TD([[subQ2,-1.0]])],"derivedFrom":subQ1}),-1.0]])]});}
            var Q9;
            {var subQ0=sQuery(id+"F14.wireOp",EDGE,"E38.7.1");var subQ1=sQuery(id+"F14.wireOp",EDGE,"E36");var subQ2=makeQuery(id+"F14.imprint","INTERSECT",VERTEX,{"disambiguationData":[OD(0.0)],"derivedFrom":[subQ1,subQ0]});Q9=makeQuery(id+"F14.imprint","IMPRINT",FACE,{"disambiguationData":[TD([[makeQuery(id+"F14.imprint","IMPRINT",EDGE,{"disambiguationData":[TD([[subQ2,-1.0]])],"derivedFrom":subQ1}),1.0]])]});}
            var Q10;
            {var subQ0=sQuery(id+"F14.wireOp",EDGE,"E36");var subQ1=sQuery(id+"F14.wireOp",EDGE,"E38.2.1");var subQ2=makeQuery(id+"F14.imprint","INTERSECT",VERTEX,{"disambiguationData":[OD(0.0)],"derivedFrom":[subQ1,subQ0]});Q10=makeQuery(id+"F14.imprint","IMPRINT",FACE,{"disambiguationData":[TD([[makeQuery(id+"F14.imprint","IMPRINT",EDGE,{"disambiguationData":[TD([[subQ2,-1.0]])],"derivedFrom":subQ1}),1.0]])]});}
            var Q11;
            {var subQ0=sQuery(id+"F14.wireOp",EDGE,"E36");var subQ1=sQuery(id+"F14.wireOp",EDGE,"E38.2.1");var subQ2=makeQuery(id+"F14.imprint","INTERSECT",VERTEX,{"disambiguationData":[OD(0.0)],"derivedFrom":[subQ1,subQ0]});Q11=makeQuery(id+"F14.imprint","IMPRINT",FACE,{"disambiguationData":[TD([[makeQuery(id+"F14.imprint","IMPRINT",EDGE,{"disambiguationData":[TD([[subQ2,1.0]])],"derivedFrom":subQ1}),1.0]])]});}
            var Q12;
            {var subQ0=sQuery(id+"F14.wireOp",EDGE,"E36");var subQ1=sQuery(id+"F14.wireOp",EDGE,"E38.1.1");var subQ2=makeQuery(id+"F14.imprint","INTERSECT",VERTEX,{"disambiguationData":[OD(0.0)],"derivedFrom":[subQ1,subQ0]});Q12=makeQuery(id+"F14.imprint","IMPRINT",FACE,{"disambiguationData":[TD([[makeQuery(id+"F14.imprint","IMPRINT",EDGE,{"disambiguationData":[TD([[subQ2,1.0]])],"derivedFrom":subQ1}),1.0]])]});}
            var Q13;
            {var subQ0=sQuery(id+"F14.wireOp",EDGE,"E36");var subQ1=sQuery(id+"F14.wireOp",EDGE,"E38.1.1");var subQ2=makeQuery(id+"F14.imprint","INTERSECT",VERTEX,{"disambiguationData":[OD(0.0)],"derivedFrom":[subQ1,subQ0]});Q13=makeQuery(id+"F14.imprint","IMPRINT",FACE,{"disambiguationData":[TD([[makeQuery(id+"F14.imprint","IMPRINT",EDGE,{"disambiguationData":[TD([[subQ2,-1.0]])],"derivedFrom":subQ1}),1.0]])]});}
            var Q14;
            {var subQ0=sQuery(id+"F14.wireOp",EDGE,"E36");var subQ1=sQuery(id+"F14.wireOp",EDGE,"E37");var subQ2=makeQuery(id+"F14.imprint","INTERSECT",VERTEX,{"disambiguationData":[OD(0.0)],"derivedFrom":[subQ1,subQ0]});Q14=makeQuery(id+"F14.imprint","IMPRINT",FACE,{"disambiguationData":[TD([[makeQuery(id+"F14.imprint","IMPRINT",EDGE,{"disambiguationData":[TD([[subQ2,1.0]])],"derivedFrom":subQ1}),1.0]])]});}
            var Q15;
            {var subQ0=sQuery(id+"F14.wireOp",EDGE,"E36");var subQ1=sQuery(id+"F14.wireOp",EDGE,"E37");var subQ2=makeQuery(id+"F14.imprint","INTERSECT",VERTEX,{"disambiguationData":[OD(0.0)],"derivedFrom":[subQ1,subQ0]});Q15=makeQuery(id+"F14.imprint","IMPRINT",FACE,{"disambiguationData":[TD([[makeQuery(id+"F14.imprint","IMPRINT",EDGE,{"disambiguationData":[TD([[subQ2,-1.0]])],"derivedFrom":subQ1}),1.0]])]});}
            extrude(context, id + "F22", {"entities" : qUnion([Q0, Q1, Q2, Q3, Q4, Q5, Q6, Q7, Q8, Q9, Q10, Q11, Q12, Q13, Q14, Q15]), "operationType" : NewBodyOperationType.REMOVE, "oppositeDirection" : true, "depth" : 25 * mm});
        }
    });
